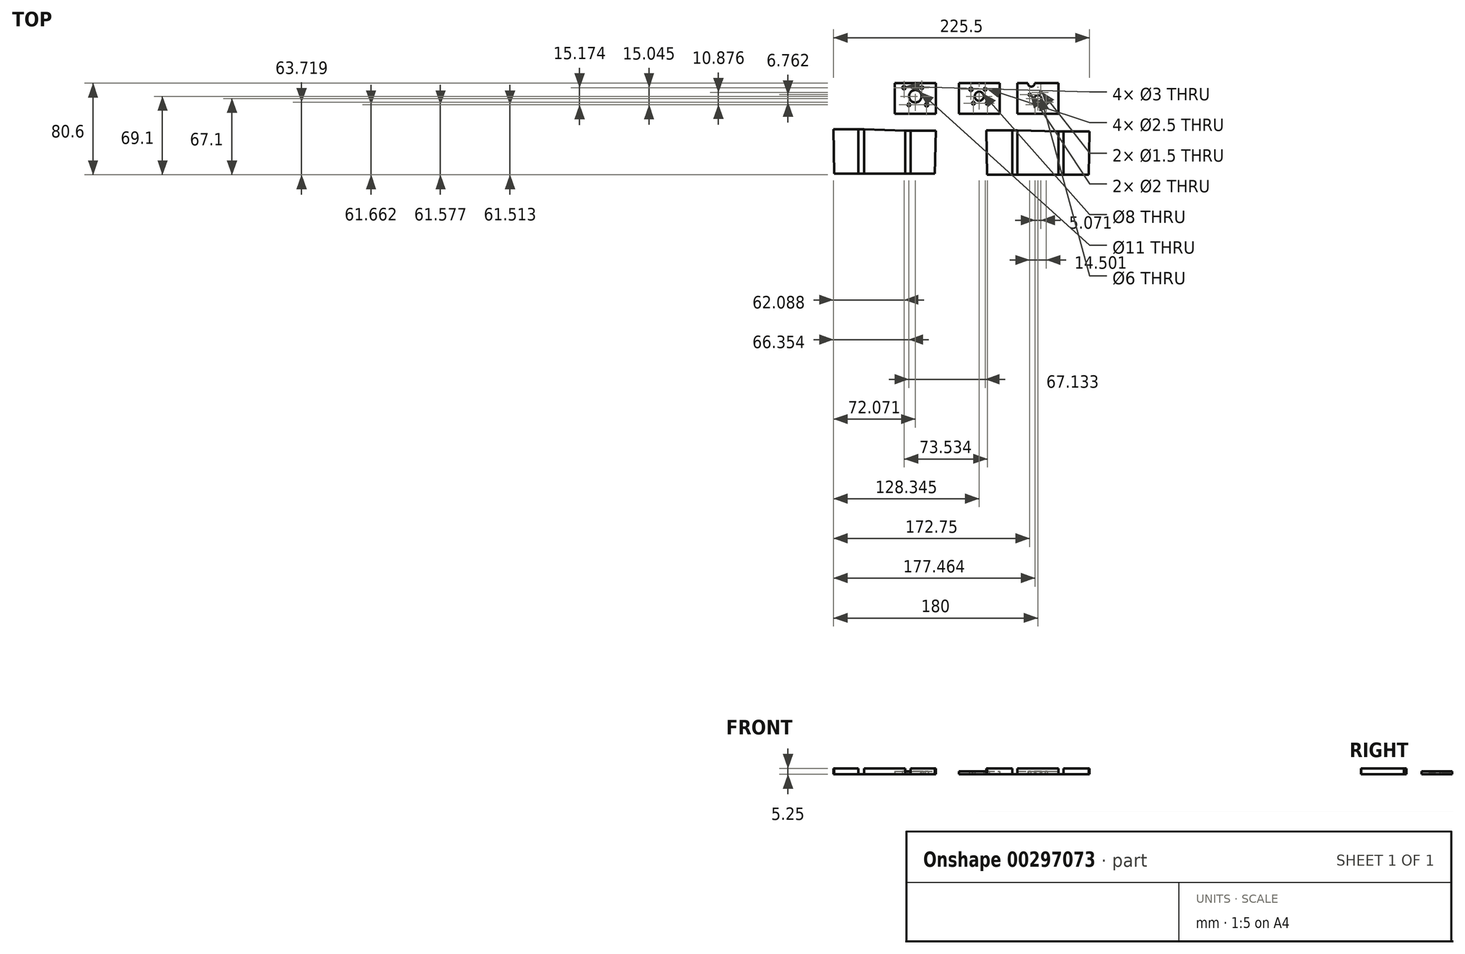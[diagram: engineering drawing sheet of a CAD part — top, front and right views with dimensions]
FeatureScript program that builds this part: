
annotation { "Feature Type Name" : "Feature", "Feature Type Description" : "" }
export const myFeature = defineFeature(function(context is Context, id is Id, definition is map)
    precondition{}
    {
        {
            assignVariable(context, id + "F0", {"name" : "foam_th", "anyValue" : 5.15 * mm});
        }
        {
            assignVariable(context, id + "F1", {"name" : "foam_th_p", "anyValue" : 5 * mm});
        }
        {
            var Q0;
            Q0=qCreatedBy(makeId("Top.planeOp"),FACE);
            var sketch = newSketch(context, id + "F2", { "sketchPlane" : qUnion([Q0])});
            skLineSegment(sketch, "E0.bottom", {"start": v(0, 0) * mm, "end": v(36, 0) * mm});
            skLineSegment(sketch, "E0.top", {"start": v(0, 27) * mm, "end": v(9.15, 27) * mm});
            skLineSegment(sketch, "E0.left", {"start": v(0, 0) * mm, "end": v(0, 27) * mm});
            skLineSegment(sketch, "E0.right", {"start": v(36, 0) * mm, "end": v(36, 27) * mm});
            skPoint(sketch, "E1", {"position": v(18, 13.5) * mm});
            skLineSegment(sketch, "E2.bottom", {"start": v(27.79, 15.56) * mm, "end": v(13.29, 22.32) * mm, "construction": true});
            skLineSegment(sketch, "E2.top", {"start": v(22.71, 4.68) * mm, "end": v(8.21, 11.44) * mm, "construction": true});
            skLineSegment(sketch, "E2.left", {"start": v(27.79, 15.56) * mm, "end": v(22.71, 4.68) * mm, "construction": true});
            skLineSegment(sketch, "E2.right", {"start": v(13.29, 22.32) * mm, "end": v(8.21, 11.44) * mm, "construction": true});
            skCircle(sketch, "E3", {"center": v(20.54, 18.94) * mm, "radius": 0.75 * mm});
            skCircle(sketch, "E4", {"center": v(25.25, 10.12) * mm, "radius": 1 * mm});
            skCircle(sketch, "E5", {"center": v(10.75, 16.88) * mm, "radius": 1 * mm});
            skCircle(sketch, "E6", {"center": v(15.46, 8.06) * mm, "radius": 0.75 * mm});
            skCircle(sketch, "E7", {"center": v(18, 13.5) * mm, "radius": 3 * mm});
            skLineSegment(sketch, "E8.0", {"start": v(5.15, 5.15) * mm, "end": v(5.15, 27) * mm, "construction": true});
            skLineSegment(sketch, "E8.1", {"start": v(5.15, 5.15) * mm, "end": v(30.85, 5.15) * mm, "construction": true});
            skLineSegment(sketch, "E8.2", {"start": v(30.85, 5.15) * mm, "end": v(30.85, 27) * mm, "construction": true});
            skArc(sketch, "E9", {"start": v(9.15, 27) * mm, "mid": v(12.15, 24) * mm, "end": v(15.15, 27) * mm});
            skLineSegment(sketch, "E10.trimOffspring", {"start": v(30.85, 27) * mm, "end": v(36, 27) * mm});
            skCircle(sketch, "E11", {"center": v(20.54, 18.94) * mm, "radius": 1.9 * mm, "construction": true});
            skCircle(sketch, "E12", {"center": v(10.75, 16.88) * mm, "radius": 1.9 * mm, "construction": true});
            skCircle(sketch, "E13", {"center": v(25.25, 10.12) * mm, "radius": 1.9 * mm, "construction": true});
            skCircle(sketch, "E14", {"center": v(15.46, 8.06) * mm, "radius": 1.9 * mm, "construction": true});
            skLineSegment(sketch, "E15", {"start": v(13.29, 22.32) * mm, "end": v(22.71, 4.68) * mm, "construction": true});
            skLineSegment(sketch, "E16", {"start": v(18, 0) * mm, "end": v(18, 27) * mm, "construction": true});
            skLineSegment(sketch, "E17", {"start": v(30.85, 27) * mm, "end": v(15.15, 27) * mm});
            skCircle(sketch, "E18", {"center": v(18, 13.5) * mm, "radius": 11.5 * mm, "construction": true});
            skLineSegment(sketch, "E19", {"start": v(9.15, 27) * mm, "end": v(15.15, 27) * mm});
            skSolve(sketch);
        }
        {
            var Q0;
            Q0=qCreatedBy(makeId("Top.planeOp"),FACE);
            var sketch = newSketch(context, id + "F3", { "sketchPlane" : qUnion([Q0])});
            skLineSegment(sketch, "E20.bottom", {"start": v(-51.65, 0) * mm, "end": v(-15.65, 0) * mm});
            skLineSegment(sketch, "E20.top", {"start": v(-51.65, 27) * mm, "end": v(-39, 27) * mm});
            skLineSegment(sketch, "E20.left", {"start": v(-51.65, 0) * mm, "end": v(-51.65, 27) * mm});
            skLineSegment(sketch, "E20.right", {"start": v(-15.65, 0) * mm, "end": v(-15.65, 27) * mm});
            skPoint(sketch, "E21", {"position": v(-33.65, 15.5) * mm});
            skLineSegment(sketch, "E22.bottom", {"start": v(-35.8, 27.73) * mm, "end": v(-46.07, 15.48) * mm, "construction": true});
            skLineSegment(sketch, "E22.top", {"start": v(-21.24, 15.52) * mm, "end": v(-31.52, 3.27) * mm, "construction": true});
            skLineSegment(sketch, "E22.left", {"start": v(-35.8, 27.73) * mm, "end": v(-21.24, 15.52) * mm, "construction": true});
            skLineSegment(sketch, "E22.right", {"start": v(-46.07, 15.48) * mm, "end": v(-31.52, 3.27) * mm, "construction": true});
            skCircle(sketch, "E23", {"center": v(-40.93, 21.6) * mm, "radius": 1.5 * mm});
            skCircle(sketch, "E24", {"center": v(-28.51, 21.63) * mm, "radius": 1.25 * mm});
            skCircle(sketch, "E25", {"center": v(-38.8, 9.37) * mm, "radius": 1.25 * mm});
            skCircle(sketch, "E26", {"center": v(-26.38, 9.4) * mm, "radius": 1.5 * mm});
            skCircle(sketch, "E27", {"center": v(-33.65, 15.5) * mm, "radius": 4 * mm});
            skLineSegment(sketch, "E28.0", {"start": v(-46.5, 5.15) * mm, "end": v(-46.5, 27) * mm, "construction": true});
            skLineSegment(sketch, "E28.1", {"start": v(-46.5, 5.15) * mm, "end": v(-20.8, 5.15) * mm, "construction": true});
            skLineSegment(sketch, "E28.2", {"start": v(-20.8, 5.15) * mm, "end": v(-20.8, 27) * mm, "construction": true});
            skArc(sketch, "E29", {"start": v(-39, 27) * mm, "mid": v(-35.5, 23.5) * mm, "end": v(-32, 27) * mm});
            skLineSegment(sketch, "E30.trimOffspring", {"start": v(-20.8, 27) * mm, "end": v(-15.65, 27) * mm});
            skCircle(sketch, "E31", {"center": v(-40.93, 21.6) * mm, "radius": 2.75 * mm, "construction": true});
            skCircle(sketch, "E32", {"center": v(-38.8, 9.37) * mm, "radius": 2.75 * mm, "construction": true});
            skCircle(sketch, "E33", {"center": v(-28.51, 21.63) * mm, "radius": 2.75 * mm, "construction": true});
            skCircle(sketch, "E34", {"center": v(-26.38, 9.4) * mm, "radius": 2.75 * mm, "construction": true});
            skLineSegment(sketch, "E35", {"start": v(-46.07, 15.48) * mm, "end": v(-21.24, 15.52) * mm, "construction": true});
            skLineSegment(sketch, "E36", {"start": v(-33.65, 0) * mm, "end": v(-33.65, 27) * mm, "construction": true});
            skPoint(sketch, "E37", {"position": v(-33.65, 13.5) * mm});
            skLineSegment(sketch, "E38", {"start": v(-32, 27) * mm, "end": v(-20.8, 27) * mm});
            skCircle(sketch, "E39", {"center": v(-33.65, 15.5) * mm, "radius": 14.5 * mm, "construction": true});
            skLineSegment(sketch, "E40", {"start": v(-39, 27) * mm, "end": v(-32, 27) * mm});
            skSolve(sketch);
        }
        {
            var Q0;
            Q0=qCreatedBy(makeId("Top.planeOp"),FACE);
            var sketch = newSketch(context, id + "F4", { "sketchPlane" : qUnion([Q0])});
            skLineSegment(sketch, "E41.bottom", {"start": v(-107.93, 0) * mm, "end": v(-71.93, 0) * mm});
            skLineSegment(sketch, "E41.top", {"start": v(-107.93, 27) * mm, "end": v(-96.78, 27) * mm});
            skLineSegment(sketch, "E41.left", {"start": v(-107.93, 0) * mm, "end": v(-107.93, 27) * mm});
            skLineSegment(sketch, "E41.right", {"start": v(-71.93, 0) * mm, "end": v(-71.93, 27) * mm});
            skPoint(sketch, "E42", {"position": v(-89.93, 15.5) * mm});
            skLineSegment(sketch, "E43.bottom", {"start": v(-94.2, 30.6) * mm, "end": v(-105.63, 15.44) * mm, "construction": true});
            skLineSegment(sketch, "E43.top", {"start": v(-74.23, 15.56) * mm, "end": v(-85.66, 0.4) * mm, "construction": true});
            skLineSegment(sketch, "E43.left", {"start": v(-94.2, 30.6) * mm, "end": v(-74.23, 15.56) * mm, "construction": true});
            skLineSegment(sketch, "E43.right", {"start": v(-105.63, 15.44) * mm, "end": v(-85.66, 0.4) * mm, "construction": true});
            skCircle(sketch, "E44", {"center": v(-99.91, 23.02) * mm, "radius": 1.5 * mm});
            skCircle(sketch, "E45", {"center": v(-84.21, 23.09) * mm, "radius": 1.25 * mm});
            skCircle(sketch, "E46", {"center": v(-95.65, 7.91) * mm, "radius": 1.25 * mm});
            skCircle(sketch, "E47", {"center": v(-79.95, 7.98) * mm, "radius": 1.5 * mm});
            skCircle(sketch, "E48", {"center": v(-89.93, 15.5) * mm, "radius": 5.5 * mm});
            skLineSegment(sketch, "E49.0", {"start": v(-102.78, 5.15) * mm, "end": v(-102.78, 27) * mm, "construction": true});
            skLineSegment(sketch, "E49.1", {"start": v(-102.78, 5.15) * mm, "end": v(-77.08, 5.15) * mm, "construction": true});
            skLineSegment(sketch, "E49.2", {"start": v(-77.08, 5.15) * mm, "end": v(-77.08, 27) * mm, "construction": true});
            skArc(sketch, "E50", {"start": v(-96.78, 27) * mm, "mid": v(-92.78, 23) * mm, "end": v(-88.78, 27) * mm});
            skLineSegment(sketch, "E51.trimOffspring", {"start": v(-77.08, 27) * mm, "end": v(-71.93, 27) * mm});
            skCircle(sketch, "E52", {"center": v(-99.91, 23.02) * mm, "radius": 2.75 * mm, "construction": true});
            skCircle(sketch, "E53", {"center": v(-95.65, 7.91) * mm, "radius": 2.75 * mm, "construction": true});
            skCircle(sketch, "E54", {"center": v(-84.21, 23.09) * mm, "radius": 2.75 * mm, "construction": true});
            skCircle(sketch, "E55", {"center": v(-79.95, 7.98) * mm, "radius": 2.75 * mm, "construction": true});
            skLineSegment(sketch, "E56", {"start": v(-105.63, 15.44) * mm, "end": v(-74.23, 15.56) * mm, "construction": true});
            skLineSegment(sketch, "E57", {"start": v(-89.93, 0) * mm, "end": v(-89.93, 27) * mm, "construction": true});
            skPoint(sketch, "E58", {"position": v(-89.93, 13.5) * mm});
            skLineSegment(sketch, "E59", {"start": v(-88.78, 27) * mm, "end": v(-77.08, 27) * mm});
            skCircle(sketch, "E60", {"center": v(-89.93, 15.5) * mm, "radius": 17.5 * mm, "construction": true});
            skLineSegment(sketch, "E61", {"start": v(-96.78, 27) * mm, "end": v(-88.78, 27) * mm});
            skSolve(sketch);
        }
        {
            var Q0;
            Q0=qCreatedBy(makeId("Top.planeOp"),FACE);
            var sketch = newSketch(context, id + "F5", { "sketchPlane" : qUnion([Q0])});
            skLineSegment(sketch, "E62.bottom", {"start": v(-134.98, -14.7) * mm, "end": v(-98.98, -14.7) * mm, "construction": true});
            skLineSegment(sketch, "E62.top", {"start": v(-134.98, -52.7) * mm, "end": v(-98.98, -52.7) * mm});
            skLineSegment(sketch, "E62.left", {"start": v(-134.98, -14.7) * mm, "end": v(-134.98, -52.7) * mm});
            skLineSegment(sketch, "E62.right", {"start": v(-98.98, -14.7) * mm, "end": v(-98.98, -52.7) * mm});
            skLineSegment(sketch, "E63.bottom", {"start": v(-139.98, -52.7) * mm, "end": v(-161.98, -52.7) * mm});
            skLineSegment(sketch, "E63.top", {"start": v(-139.98, -14.7) * mm, "end": v(-161.98, -14.7) * mm, "construction": true});
            skLineSegment(sketch, "E63.left", {"start": v(-139.98, -52.7) * mm, "end": v(-139.98, -14.7) * mm});
            skLineSegment(sketch, "E63.right", {"start": v(-161.98, -52.7) * mm, "end": v(-161.98, -14.7) * mm, "construction": true});
            skLineSegment(sketch, "E64.bottom", {"start": v(-93.98, -52.7) * mm, "end": v(-71.98, -52.7) * mm});
            skLineSegment(sketch, "E64.top", {"start": v(-93.98, -14.7) * mm, "end": v(-71.98, -14.7) * mm});
            skLineSegment(sketch, "E64.left", {"start": v(-93.98, -52.7) * mm, "end": v(-93.98, -14.7) * mm});
            skLineSegment(sketch, "E64.right", {"start": v(-71.98, -52.7) * mm, "end": v(-71.98, -14.7) * mm, "construction": true});
            skLineSegment(sketch, "E65", {"start": v(-139.98, -14.7) * mm, "end": v(-134.98, -14.7) * mm, "construction": true});
            skLineSegment(sketch, "E66", {"start": v(-98.98, -14.7) * mm, "end": v(-93.98, -14.7) * mm});
            skLineSegment(sketch, "E67", {"start": v(-98.98, -52.7) * mm, "end": v(-93.98, -52.7) * mm});
            skLineSegment(sketch, "E68", {"start": v(-139.98, -52.7) * mm, "end": v(-134.98, -52.7) * mm});
            skLineSegment(sketch, "E69", {"start": v(-98.98, -14.7) * mm, "end": v(-134.98, -13.45) * mm});
            skLineSegment(sketch, "E70", {"start": v(-134.98, -13.45) * mm, "end": v(-139.98, -13.45) * mm});
            skLineSegment(sketch, "E71", {"start": v(-139.98, -13.45) * mm, "end": v(-161.98, -13.45) * mm});
            skLineSegment(sketch, "E72", {"start": v(-161.98, -13.45) * mm, "end": v(-161.98, -14.7) * mm, "construction": true});
            skLineSegment(sketch, "E73", {"start": v(-139.98, -14.7) * mm, "end": v(-139.98, -13.45) * mm});
            skLineSegment(sketch, "E74", {"start": v(-134.98, -14.7) * mm, "end": v(-134.98, -13.45) * mm});
            skLineSegment(sketch, "E75", {"start": v(-71.98, -14.7) * mm, "end": v(-72.65, -52.7) * mm});
            skLineSegment(sketch, "E76", {"start": v(-161.98, -14.7) * mm, "end": v(-161.32, -52.7) * mm});
            skLineSegment(sketch, "E77", {"start": v(-161.98, -14.7) * mm, "end": v(-162, -13.45) * mm});
            skLineSegment(sketch, "E78", {"start": v(-162, -13.45) * mm, "end": v(-161.98, -13.45) * mm});
            skSolve(sketch);
        }
        {
            var Q0;
            Q0=qCreatedBy(makeId("Top.planeOp"),FACE);
            var sketch = newSketch(context, id + "F6", { "sketchPlane" : qUnion([Q0])});
            skLineSegment(sketch, "E79.bottom", {"start": v(0, -15.6) * mm, "end": v(36, -15.6) * mm, "construction": true});
            skLineSegment(sketch, "E79.top", {"start": v(0, -53.6) * mm, "end": v(36, -53.6) * mm});
            skLineSegment(sketch, "E79.left", {"start": v(0, -15.6) * mm, "end": v(0, -53.6) * mm});
            skLineSegment(sketch, "E79.right", {"start": v(36, -15.6) * mm, "end": v(36, -53.6) * mm});
            skLineSegment(sketch, "E80.bottom", {"start": v(-4.65, -53.6) * mm, "end": v(-27.5, -53.6) * mm});
            skLineSegment(sketch, "E80.top", {"start": v(-4.65, -15.6) * mm, "end": v(-27.5, -15.6) * mm, "construction": true});
            skLineSegment(sketch, "E80.left", {"start": v(-4.65, -53.6) * mm, "end": v(-4.65, -15.6) * mm});
            skLineSegment(sketch, "E80.right", {"start": v(-27.5, -53.6) * mm, "end": v(-27.5, -15.6) * mm, "construction": true});
            skLineSegment(sketch, "E81.bottom", {"start": v(40.65, -53.6) * mm, "end": v(63.5, -53.6) * mm});
            skLineSegment(sketch, "E81.top", {"start": v(40.65, -15.6) * mm, "end": v(63.5, -15.6) * mm});
            skLineSegment(sketch, "E81.left", {"start": v(40.65, -53.6) * mm, "end": v(40.65, -15.6) * mm});
            skLineSegment(sketch, "E81.right", {"start": v(63.5, -53.6) * mm, "end": v(63.5, -15.6) * mm, "construction": true});
            skLineSegment(sketch, "E82", {"start": v(-4.65, -15.6) * mm, "end": v(0, -15.6) * mm, "construction": true});
            skLineSegment(sketch, "E83", {"start": v(36, -15.6) * mm, "end": v(40.65, -15.6) * mm});
            skLineSegment(sketch, "E84", {"start": v(36, -53.6) * mm, "end": v(40.65, -53.6) * mm});
            skLineSegment(sketch, "E85", {"start": v(-4.65, -53.6) * mm, "end": v(0, -53.6) * mm});
            skLineSegment(sketch, "E86", {"start": v(36, -15.6) * mm, "end": v(0, -14.34) * mm});
            skLineSegment(sketch, "E87", {"start": v(0, -14.34) * mm, "end": v(-4.65, -14.34) * mm});
            skLineSegment(sketch, "E88", {"start": v(-4.65, -14.34) * mm, "end": v(-27.5, -14.34) * mm});
            skLineSegment(sketch, "E89", {"start": v(-27.5, -14.34) * mm, "end": v(-27.5, -15.6) * mm, "construction": true});
            skLineSegment(sketch, "E90", {"start": v(-4.65, -15.6) * mm, "end": v(-4.65, -14.34) * mm});
            skLineSegment(sketch, "E91", {"start": v(0, -15.6) * mm, "end": v(0, -14.34) * mm});
            skLineSegment(sketch, "E92", {"start": v(63.5, -15.6) * mm, "end": v(62.84, -53.6) * mm});
            skLineSegment(sketch, "E93", {"start": v(-27.5, -15.6) * mm, "end": v(-26.84, -53.6) * mm});
            skLineSegment(sketch, "E94", {"start": v(-27.5, -15.6) * mm, "end": v(-27.52, -14.34) * mm});
            skLineSegment(sketch, "E95", {"start": v(-27.52, -14.34) * mm, "end": v(-27.5, -14.34) * mm});
            skSolve(sketch);
        }
        {
            var Q0;
            Q0=makeQuery(id+"F2.imprint","IMPRINT",FACE,{"disambiguationData":[TD([[makeQuery(id+"F2.imprint","IMPRINT",EDGE,{"derivedFrom":sQuery(id+"F2.wireOp",EDGE,"E0.bottom")}),1.0]])]});
            var Q1;
            Q1=makeQuery(id+"F3.imprint","IMPRINT",FACE,{"disambiguationData":[TD([[makeQuery(id+"F3.imprint","IMPRINT",EDGE,{"derivedFrom":sQuery(id+"F3.wireOp",EDGE,"E20.bottom")}),1.0]])]});
            var Q2;
            Q2=makeQuery(id+"F4.imprint","IMPRINT",FACE,{"disambiguationData":[TD([[makeQuery(id+"F4.imprint","IMPRINT",EDGE,{"derivedFrom":sQuery(id+"F4.wireOp",EDGE,"E41.bottom")}),1.0]])]});
            var Q3;
            Q3=makeQuery(id+"F4.imprint","IMPRINT",FACE,{"disambiguationData":[TD([[makeQuery(id+"F4.imprint","IMPRINT",EDGE,{"derivedFrom":sQuery(id+"F4.wireOp",EDGE,"E50")}),1.0]])]});
            var Q4;
            Q4=makeQuery(id+"F3.imprint","IMPRINT",FACE,{"disambiguationData":[TD([[makeQuery(id+"F3.imprint","IMPRINT",EDGE,{"derivedFrom":sQuery(id+"F3.wireOp",EDGE,"E29")}),1.0]])]});
            extrude(context, id + "F7", {"entities" : qUnion([Q0, Q1, Q2, Q3, Q4]), "depth" : 2.5 * mm});
        }
        {
            var Q0;
            {var subQ1=sQuery(id+"F6.wireOp",EDGE,"E80.left");Q0=makeQuery(id+"F6.imprint","IMPRINT",FACE,{"disambiguationData":[TD([[makeQuery(id+"F6.imprint","IMPRINT",EDGE,{"derivedFrom":subQ1}),1.0]])]});}
            var Q1;
            Q1=makeQuery(id+"F6.imprint","IMPRINT",FACE,{"disambiguationData":[TD([[makeQuery(id+"F6.imprint","IMPRINT",EDGE,{"derivedFrom":sQuery(id+"F6.wireOp",EDGE,"E79.left")}),-1.0]])]});
            var Q2;
            Q2=makeQuery(id+"F6.imprint","IMPRINT",FACE,{"disambiguationData":[TD([[makeQuery(id+"F6.imprint","IMPRINT",EDGE,{"derivedFrom":sQuery(id+"F6.wireOp",EDGE,"E79.top")}),1.0]])]});
            var Q3;
            Q3=makeQuery(id+"F6.imprint","IMPRINT",FACE,{"disambiguationData":[TD([[makeQuery(id+"F6.imprint","IMPRINT",EDGE,{"derivedFrom":sQuery(id+"F6.wireOp",EDGE,"E79.right")}),1.0]])]});
            var Q4;
            Q4=makeQuery(id+"F6.imprint","IMPRINT",FACE,{"disambiguationData":[TD([[makeQuery(id+"F6.imprint","IMPRINT",EDGE,{"derivedFrom":sQuery(id+"F6.wireOp",EDGE,"E81.top")}),-1.0]])]});
            extrude(context, id + "F8", {"entities" : qUnion([Q0, Q1, Q2, Q3, Q4]), "oppositeDirection" : true, "depth" : 0.1 * mm});
        }
        {
            var Q0;
            {var subQ1=sQuery(id+"F6.wireOp",EDGE,"E80.left");Q0=makeQuery(id+"F6.imprint","IMPRINT",FACE,{"disambiguationData":[TD([[makeQuery(id+"F6.imprint","IMPRINT",EDGE,{"derivedFrom":subQ1}),1.0]])]});}
            var Q1;
            Q1=makeQuery(id+"F6.imprint","IMPRINT",FACE,{"disambiguationData":[TD([[makeQuery(id+"F6.imprint","IMPRINT",EDGE,{"derivedFrom":sQuery(id+"F6.wireOp",EDGE,"E79.top")}),1.0]])]});
            var Q2;
            Q2=makeQuery(id+"F6.imprint","IMPRINT",FACE,{"disambiguationData":[TD([[makeQuery(id+"F6.imprint","IMPRINT",EDGE,{"derivedFrom":sQuery(id+"F6.wireOp",EDGE,"E81.top")}),-1.0]])]});
            extrude(context, id + "F9", {"entities" : qUnion([Q0, Q1, Q2]), "operationType" : NewBodyOperationType.ADD, "depth" : getVariable(context, 'foam_th')});
        }
        {
            var Q0;
            Q0=makeQuery(id+"F5.imprint","IMPRINT",FACE,{"disambiguationData":[TD([[makeQuery(id+"F5.imprint","IMPRINT",EDGE,{"derivedFrom":sQuery(id+"F5.wireOp",EDGE,"E62.left")}),-1.0]])]});
            var Q1;
            Q1=makeQuery(id+"F5.imprint","IMPRINT",FACE,{"disambiguationData":[TD([[makeQuery(id+"F5.imprint","IMPRINT",EDGE,{"derivedFrom":sQuery(id+"F5.wireOp",EDGE,"E62.right")}),1.0]])]});
            var Q2;
            {var subQ0=sQuery(id+"F5.wireOp",EDGE,"E63.left");Q2=makeQuery(id+"F5.imprint","IMPRINT",FACE,{"disambiguationData":[TD([[makeQuery(id+"F5.imprint","IMPRINT",EDGE,{"derivedFrom":subQ0}),1.0]])]});}
            var Q3;
            Q3=makeQuery(id+"F5.imprint","IMPRINT",FACE,{"disambiguationData":[TD([[makeQuery(id+"F5.imprint","IMPRINT",EDGE,{"derivedFrom":sQuery(id+"F5.wireOp",EDGE,"E62.top")}),1.0]])]});
            var Q4;
            Q4=makeQuery(id+"F5.imprint","IMPRINT",FACE,{"disambiguationData":[TD([[makeQuery(id+"F5.imprint","IMPRINT",EDGE,{"derivedFrom":sQuery(id+"F5.wireOp",EDGE,"E64.top")}),-1.0]])]});
            extrude(context, id + "F10", {"entities" : qUnion([Q0, Q1, Q2, Q3, Q4]), "depth" : 0.1 * mm});
        }
        {
            var Q0;
            {var subQ0=sQuery(id+"F5.wireOp",EDGE,"E63.left");Q0=makeQuery(id+"F5.imprint","IMPRINT",FACE,{"disambiguationData":[TD([[makeQuery(id+"F5.imprint","IMPRINT",EDGE,{"derivedFrom":subQ0}),1.0]])]});}
            var Q1;
            Q1=makeQuery(id+"F5.imprint","IMPRINT",FACE,{"disambiguationData":[TD([[makeQuery(id+"F5.imprint","IMPRINT",EDGE,{"derivedFrom":sQuery(id+"F5.wireOp",EDGE,"E62.top")}),1.0]])]});
            var Q2;
            Q2=makeQuery(id+"F5.imprint","IMPRINT",FACE,{"disambiguationData":[TD([[makeQuery(id+"F5.imprint","IMPRINT",EDGE,{"derivedFrom":sQuery(id+"F5.wireOp",EDGE,"E64.top")}),-1.0]])]});
            extrude(context, id + "F11", {"entities" : qUnion([Q0, Q1, Q2]), "depth" : getVariable(context, 'foam_th_p')});
        }
    });
